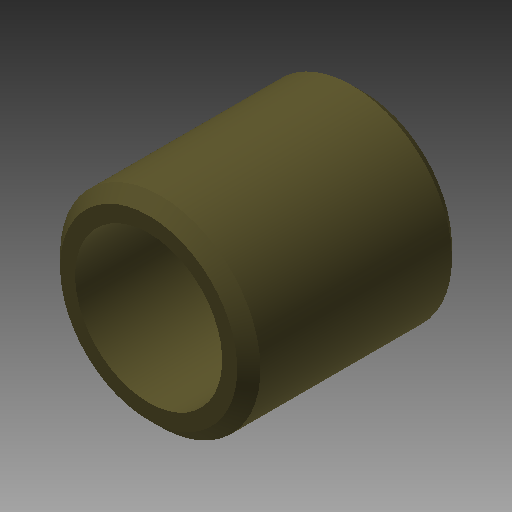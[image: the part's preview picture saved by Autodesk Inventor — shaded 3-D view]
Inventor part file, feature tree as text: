
AUTODESK INVENTOR PART (.ipt)
format: ipt  version: 2018 (Build 220112000, 112)  size: 127,488 bytes
history: native  units: in
note: dims shown in document units (in); Inventor stores cm internally (conversion verified against a paired STEP export)
features: other x35, revolve x1, sketch x1
ambient origin geometry x8: Origin, YZ Plane, XZ Plane, XY Plane, X Axis, Y Axis, Z Axis, Center Point
bodies: Solid1 (feature_tree)
feature tree (37):
  revolve  "Revolution1"  [1 undecoded]
  other  "bushing_XY"
  other  "bushing_YZ"
  other  "bushing_ZX"
  other  "bushing_X"
  other  "bushing_Y"
  other  "bushing_Z"
  other  "bushing_Center"
  other  "id1_XY"
  other  "id1_YZ"
  other  "id1_ZX"
  other  "id1_X"
  other  "id1_Y"
  other  "id1_Z"
  other  "id1_Center"
  other  "id2_XY"
  other  "id2_YZ"
  other  "id2_ZX"
  other  "id2_X"
  other  "id2_Y"
  other  "id2_Z"
  other  "id2_Center"
  other  "id3_XY"
  other  "id3_YZ"
  other  "id3_ZX"
  other  "id3_X"
  other  "id3_Y"
  other  "id3_Z"
  other  "id3_Center"
  other  "id4_XY"
  other  "id4_YZ"
  other  "id4_ZX"
  other  "id4_X"
  other  "id4_Y"
  other  "id4_Z"
  other  "id4_Center"
  sketch  "Sketch_1"  dims[d0=360.0deg d1=0.0in d2=0.0in]
note: 1 required parameter value undecoded (feature->parameter linkage not recoverable at this tier; creation-order binding heuristic only, values carry confidence <= 0.55)
